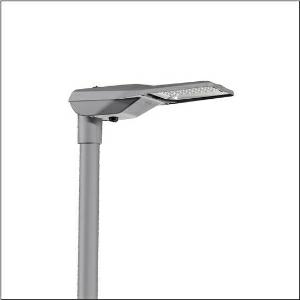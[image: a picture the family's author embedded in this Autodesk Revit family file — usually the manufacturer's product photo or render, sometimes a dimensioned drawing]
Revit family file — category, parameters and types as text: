
# Revit family: streetlight_sl_21_iq_mini___st1_0ab_5xe2m31y08jb_87eb
name_source: partatom
category: Lighting Fixtures
units: mm (PartAtom-declared; Revit-internal decimal feet)

## family parameters
Cut with Voids When Loaded = No
Host = Face
Light Source = No
Part Type = Normal
Room Calculation Point = No
Round Connector Dimension = Use Diameter
Shared = No

## types (1)
- --- (1 x LED, 9870 lm, 72.5 W, 3000K)
    Apparent Load = 73 VA
    CIE Flux Codes = 40 74 97 100 100
    Color Rendering = 70
    Color Temperature = 3000K
    Default Elevation = 1800 mm
    Description = Streetlight SL 21 iQ mini, mast luminaire, primary light control with lens, of PMMA, primary optical cover: cover, of toughened safety glass, transparent, light distribution: ST1.0aB, light emission: direct distribution, primary light characteristic: asymmetric, installation type: post-top, side-entry, LED, High Power LED, rated luminous flux: 9.870lm, luminous efficacy: 136lm/W, light colour: 730, colour temperature: 3000K, control gear: iQ-Street Remote, D4i with power reduction, control: pre-setting: logarithmic dimming characteristic, Street-Remote, Auto-Match, Temp-Guard, Lumen-Switch, Night-Set, Smart-Wire, Light-Fading, Desk-Remote (wireless, voltage-free reading and setting of iQ features in the workshop via application-optimized NFC function/RFID function), optimised constant luminous flux control (CLO 2.0), mains connection: 220..240V, AC, 50/60Hz, start of lifetime: 73W, end of service life: 76W, reduction: 33W, luminaire housing, of diecast aluminium, powder-coated, Siteco® metallic grey (DB 702S), corrosivity category C5 mid according to DIN EN ISO 12944, please order mast flange separately, inclination adjustable: 0°, 5°, 10°, 15°, sealing non-destructively replaceable, multi-level sealing system, length: 628mm, width: 235mm, height: 110mm, mast flange for spigot size: 42mm (side-entry): 5XC10008XM4, 60/48mm (side-entry/post-top): 5XC10108XM2, 76/60mm (side-entry/post-top): 5XC10108XM1, mounting height: 4..8m, Smart Interface below and above, protection rating (complete): IP66, insulation class (complete): insulation class II (safety insulation), certification: CE, ENEC, ENEC+, VDE, impact resistance: IK10, permissible operating ambient temperature for outdoor applications: -40..+50°C, standard-compliant lighting for roads and squares, packaging unit: 1 piece

Light Distribution: ST1.0aB
    Height = 110 mm
    Lamp = 1 x LED
    Lamp Light Flux = 9870 lm
    Lamp Power = 72.5 W
    Lamp count = 1
    Length = 625 mm
    Luminous efficacy = 136 lm/W
    Manufacturer = Siteco
    ModVariant = No
    Model = 5XE2M31Y08JB
    Number of Poles = 1
    OnlyDefault = Yes
    Power Factor = 1
    Product Name = Streetlight SL 21 iQ mini | ST1.0aB
    Product group = mast luminaire | pylon top
    ProductGroupID = 6100
    Protection Class = Protection class II
    Protection Degree = IP 66
    RLX_Detail_Level = 1
    RLX_Emergency_Light_Flux = 0 lm
    RLX_Emergency_Type = 0
    RLX_Emergency_Type_DB = No
    RlxData = <blob elided: 26669 chars, md5=2595616b>
    Socket = socket
    Standby Power = 0 W
    System Light Flux = 9870 lm
    System Power = 73 W
    Type Comments = factory setting: luminous flux: 100 % | dim-lin: 254 | 755 mA
    Type Image = l_1003514.jpg
    URL = http://relux.com
    VarID = @adj_112172
    Voltage = 0 V
    Weight = 0.00 kg
    Width = 234 mm

## geometry (parser evidence)
native form markers: Blend x4, Sweep x10
no freeform markers — native parametric forms only
